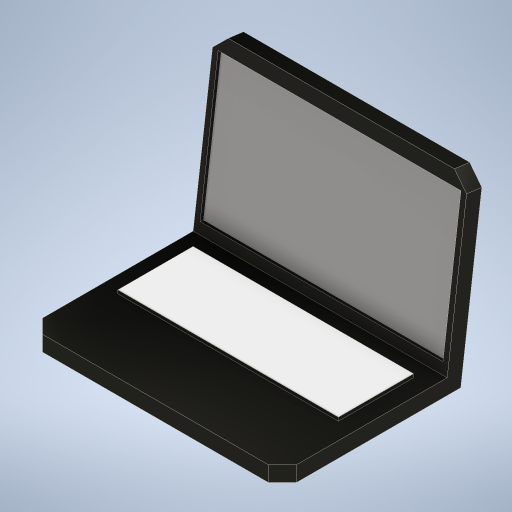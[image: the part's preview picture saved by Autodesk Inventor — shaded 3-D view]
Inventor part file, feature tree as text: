
AUTODESK INVENTOR PART (.ipt)
format: ipt  version: 2024 (Build 280153000, 153)  size: 264,192 bytes
history: native  units: in
note: dims shown in document units (in); Inventor stores cm internally (conversion verified against a paired STEP export)
features: extrude x3, sketch x3, chamfer x1, other x1
ambient origin geometry x8: Origin, YZ Plane, XZ Plane, XY Plane, X Axis, Y Axis, Z Axis, Center Point
bodies: Solid1 (feature_tree)
feature tree (8):
  extrude  "Extrusion1"  Depth=10.0394in
  chamfer  "Chamfer1"  Distance=14.3071in
  extrude  "Extrusion2"  Depth=0.7874in TaperAngle=45.0deg
  extrude  "Extrusion3"  Depth=0.315in
  sketch  "Sketch1"  dims[d0=0.8661in d1=10.0394in]
  sketch  "Sketch2"  dims[d2=0.8661in]
  sketch  "Sketch4"  dims[d3=10.0394in d4=14.3071in d5=0.0in d6=0.7874in d7=0.0787in d8=45.0deg d9=0.315in d10=0.315in d11=0.7874in d12=0.5906in d13=0.1969in d14=0.0in d15=1.0236in d16=0.9449in d17=0.9449in d18=4.0945in d19=0.1969in d20=0.0in]
  other  "Finish1"
